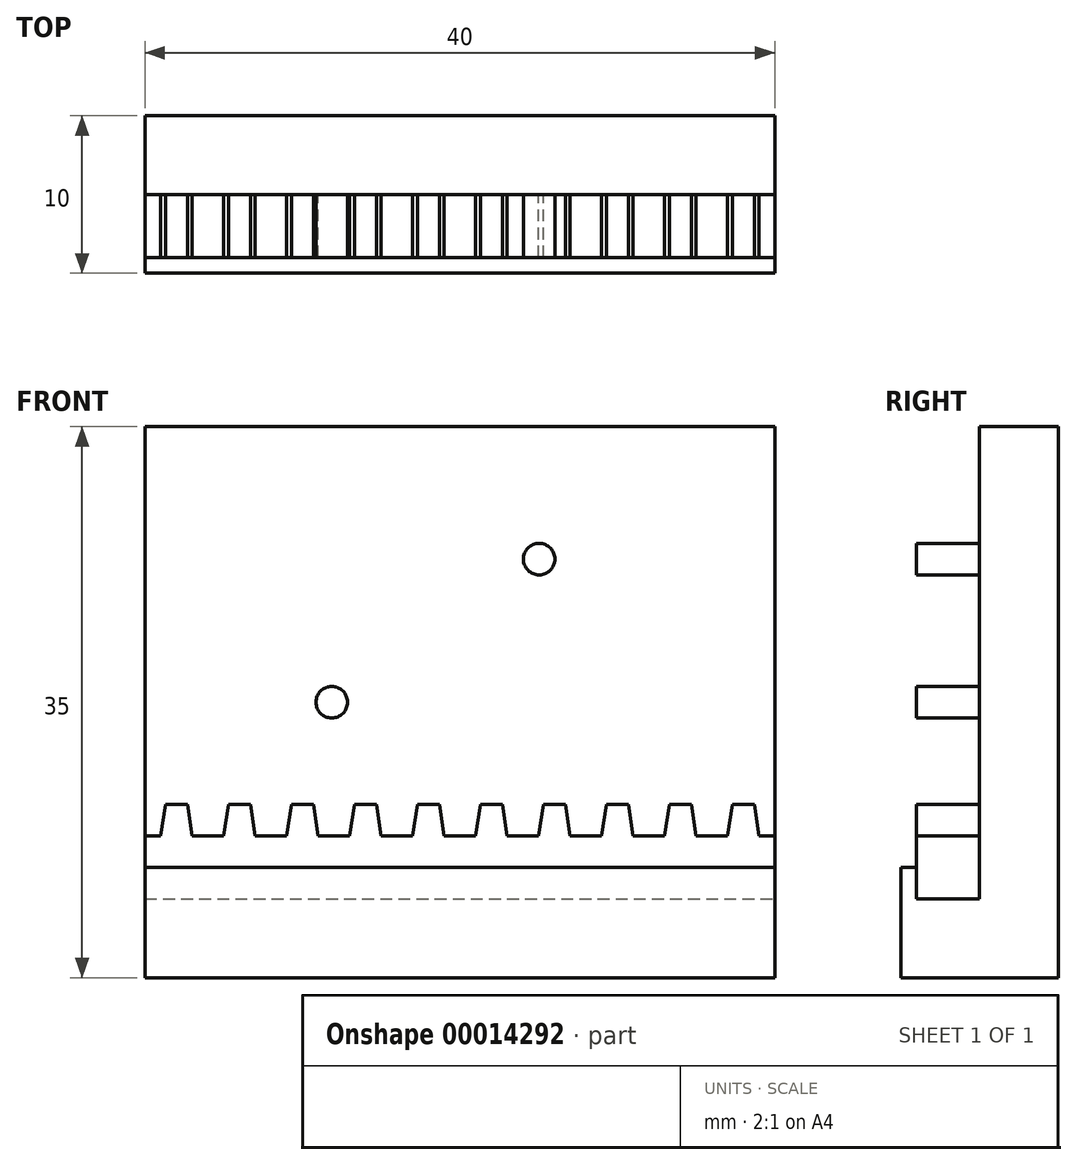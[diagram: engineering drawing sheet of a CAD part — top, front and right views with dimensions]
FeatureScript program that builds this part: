
annotation { "Feature Type Name" : "Feature", "Feature Type Description" : "" }
export const myFeature = defineFeature(function(context is Context, id is Id, definition is map)
    precondition{}
    {
        {
            var Q0;
            Q0=qCreatedBy(makeId("Front.planeOp"),FACE);
            var sketch = newSketch(context, id + "F0", { "sketchPlane" : qUnion([Q0])});
            skLineSegment(sketch, "E0.rect.bottom", {"start": v(20, -17.5) * mm, "end": v(-20, -17.5) * mm});
            skLineSegment(sketch, "E0.rect.top", {"start": v(20, 17.5) * mm, "end": v(-20, 17.5) * mm});
            skLineSegment(sketch, "E0.rect.left", {"start": v(20, -17.5) * mm, "end": v(20, 17.5) * mm});
            skLineSegment(sketch, "E0.rect.right", {"start": v(-20, -17.5) * mm, "end": v(-20, 17.5) * mm});
            skPoint(sketch, "E0.rect.middle", {"position": v(0, 0) * mm});
            skSolve(sketch);
        }
        {
            var Q0;
            Q0 = qSketchRegion(id + "F0", true);
            extrude(context, id + "F1", {"entities" : qUnion([Q0]), "depth" : 10 * mm});
        }
        {
            var Q0;
            Q0=makeQuery(id+"F1.opExtrude","CAP_FACE",FACE,{"disambiguationData":[OSD([sQuery(id+"F0.wireOp",EDGE,"E0.rect.bottom"),sQuery(id+"F0.wireOp",EDGE,"E0.rect.top"),sQuery(id+"F0.wireOp",EDGE,"E0.rect.left"),sQuery(id+"F0.wireOp",EDGE,"E0.rect.right")])],"isStart":false});
            var sketch = newSketch(context, id + "F2", { "sketchPlane" : qUnion([Q0])});
            skLineSegment(sketch, "E1.bottom", {"start": v(-20, 17.5) * mm, "end": v(20, 17.5) * mm});
            skLineSegment(sketch, "E1.top", {"start": v(-20, -12.5) * mm, "end": v(20, -12.5) * mm});
            skLineSegment(sketch, "E1.left", {"start": v(-20, 17.5) * mm, "end": v(-20, -12.5) * mm});
            skLineSegment(sketch, "E1.right", {"start": v(20, 17.5) * mm, "end": v(20, -12.5) * mm});
            skSolve(sketch);
        }
        {
            var Q0;
            Q0 = qSketchRegion(id + "F2", true);
            extrude(context, id + "F3", {"entities" : qUnion([Q0]), "operationType" : NewBodyOperationType.REMOVE, "oppositeDirection" : true, "depth" : 5 * mm});
        }
        {
            var Q0;
            Q0=makeQuery(id+"F1.opExtrude","SWEPT_FACE",FACE,{"disambiguationData":[OSD([sQuery(id+"F0.wireOp",EDGE,"E0.rect.left")])]});
            var sketch = newSketch(context, id + "F4", { "sketchPlane" : qUnion([Q0])});
            skLineSegment(sketch, "E2.bottom", {"start": v(-10, -12.5) * mm, "end": v(-9, -12.5) * mm});
            skLineSegment(sketch, "E2.top", {"start": v(-10, -10.5) * mm, "end": v(-9, -10.5) * mm});
            skLineSegment(sketch, "E2.left", {"start": v(-10, -12.5) * mm, "end": v(-10, -10.5) * mm});
            skLineSegment(sketch, "E2.right", {"start": v(-9, -12.5) * mm, "end": v(-9, -10.5) * mm});
            skSolve(sketch);
        }
        {
            var Q0;
            Q0 = qSketchRegion(id + "F4", true);
            var Q1;
            Q1=makeQuery(id+"F1.opExtrude","SWEPT_FACE",FACE,{"disambiguationData":[OSD([sQuery(id+"F0.wireOp",EDGE,"E0.rect.right")])]});
            extrude(context, id + "F5", {"entities" : qUnion([Q0]), "operationType" : NewBodyOperationType.ADD, "endBound" : BoundingType.UP_TO_SURFACE, "oppositeDirection" : true, "endBoundEntityFace" : qUnion([Q1]), "depth" : 25 * mm});
        }
        {
            var Q0;
            Q0=makeQuery(id+"F3.boolean.opBoolean","COPY",FACE,{"derivedFrom":makeQuery(id+"F3.opExtrude","CAP_FACE",FACE,{"disambiguationData":[OSD([sQuery(id+"F2.wireOp",EDGE,"E1.bottom"),sQuery(id+"F2.wireOp",EDGE,"E1.top"),sQuery(id+"F2.wireOp",EDGE,"E1.left"),sQuery(id+"F2.wireOp",EDGE,"E1.right")])],"isStart":false})});
            var sketch = newSketch(context, id + "F6", { "sketchPlane" : qUnion([Q0])});
            skCircle(sketch, "E3", {"center": v(-8.14, 0) * mm, "radius": 1 * mm});
            skCircle(sketch, "E4", {"center": v(5.04, 9.09) * mm, "radius": 1 * mm});
            skSolve(sketch);
        }
        {
            var Q0;
            Q0 = qSketchRegion(id + "F6", true);
            extrude(context, id + "F7", {"entities" : qUnion([Q0]), "operationType" : NewBodyOperationType.ADD, "depth" : 4 * mm});
        }
        {
            var Q0;
            Q0=makeQuery(id+"F3.boolean.opBoolean","COPY",FACE,{"derivedFrom":makeQuery(id+"F3.opExtrude","CAP_FACE",FACE,{"disambiguationData":[OSD([sQuery(id+"F2.wireOp",EDGE,"E1.bottom"),sQuery(id+"F2.wireOp",EDGE,"E1.top"),sQuery(id+"F2.wireOp",EDGE,"E1.left"),sQuery(id+"F2.wireOp",EDGE,"E1.right")])],"isStart":false})});
            var sketch = newSketch(context, id + "F8", { "sketchPlane" : qUnion([Q0])});
            skLineSegment(sketch, "E5.bottom", {"start": v(20, -8.5) * mm, "end": v(-20, -8.5) * mm});
            skLineSegment(sketch, "E5.top", {"start": v(20, -12.5) * mm, "end": v(-20, -12.5) * mm});
            skLineSegment(sketch, "E5.left", {"start": v(20, -8.5) * mm, "end": v(20, -12.5) * mm});
            skLineSegment(sketch, "E5.right", {"start": v(-20, -8.5) * mm, "end": v(-20, -12.5) * mm});
            skLineSegment(sketch, "E6", {"start": v(-18, -8.5) * mm, "end": v(-18, -12.5) * mm, "construction": true});
            skLineSegment(sketch, "E7", {"start": v(-19, -8.5) * mm, "end": v(-18.7, -6.5) * mm});
            skLineSegment(sketch, "E8", {"start": v(-18.7, -6.5) * mm, "end": v(-18, -6.5) * mm});
            skLineSegment(sketch, "E9.MirrorCS", {"start": v(-17, -8.5) * mm, "end": v(-17.3, -6.5) * mm});
            skLineSegment(sketch, "E10.MirrorCS", {"start": v(-17.3, -6.5) * mm, "end": v(-18, -6.5) * mm});
            skLineSegment(sketch, "E11.1.0.0", {"start": v(-15, -8.5) * mm, "end": v(-14.7, -6.5) * mm});
            skLineSegment(sketch, "E11.1.0.1", {"start": v(-14.7, -6.5) * mm, "end": v(-14, -6.5) * mm});
            skLineSegment(sketch, "E11.1.0.2", {"start": v(-13.3, -6.5) * mm, "end": v(-14, -6.5) * mm});
            skLineSegment(sketch, "E11.1.0.3", {"start": v(-13, -8.5) * mm, "end": v(-13.3, -6.5) * mm});
            skLineSegment(sketch, "E11.2.0.0", {"start": v(-11, -8.5) * mm, "end": v(-10.7, -6.5) * mm});
            skLineSegment(sketch, "E11.2.0.1", {"start": v(-10.7, -6.5) * mm, "end": v(-10, -6.5) * mm});
            skLineSegment(sketch, "E11.2.0.2", {"start": v(-9.3, -6.5) * mm, "end": v(-10, -6.5) * mm});
            skLineSegment(sketch, "E11.2.0.3", {"start": v(-9, -8.5) * mm, "end": v(-9.3, -6.5) * mm});
            skLineSegment(sketch, "E11.3.0.0", {"start": v(-7, -8.5) * mm, "end": v(-6.7, -6.5) * mm});
            skLineSegment(sketch, "E11.3.0.1", {"start": v(-6.7, -6.5) * mm, "end": v(-6, -6.5) * mm});
            skLineSegment(sketch, "E11.3.0.2", {"start": v(-5.3, -6.5) * mm, "end": v(-6, -6.5) * mm});
            skLineSegment(sketch, "E11.3.0.3", {"start": v(-5, -8.5) * mm, "end": v(-5.3, -6.5) * mm});
            skLineSegment(sketch, "E11.4.0.0", {"start": v(-3, -8.5) * mm, "end": v(-2.7, -6.5) * mm});
            skLineSegment(sketch, "E11.4.0.1", {"start": v(-2.7, -6.5) * mm, "end": v(-2, -6.5) * mm});
            skLineSegment(sketch, "E11.4.0.2", {"start": v(-1.3, -6.5) * mm, "end": v(-2, -6.5) * mm});
            skLineSegment(sketch, "E11.4.0.3", {"start": v(-1, -8.5) * mm, "end": v(-1.3, -6.5) * mm});
            skLineSegment(sketch, "E11.5.0.0", {"start": v(1, -8.5) * mm, "end": v(1.3, -6.5) * mm});
            skLineSegment(sketch, "E11.5.0.1", {"start": v(1.3, -6.5) * mm, "end": v(2, -6.5) * mm});
            skLineSegment(sketch, "E11.5.0.2", {"start": v(2.7, -6.5) * mm, "end": v(2, -6.5) * mm});
            skLineSegment(sketch, "E11.5.0.3", {"start": v(3, -8.5) * mm, "end": v(2.7, -6.5) * mm});
            skLineSegment(sketch, "E11.6.0.0", {"start": v(5, -8.5) * mm, "end": v(5.3, -6.5) * mm});
            skLineSegment(sketch, "E11.6.0.1", {"start": v(5.3, -6.5) * mm, "end": v(6, -6.5) * mm});
            skLineSegment(sketch, "E11.6.0.2", {"start": v(6.7, -6.5) * mm, "end": v(6, -6.5) * mm});
            skLineSegment(sketch, "E11.6.0.3", {"start": v(7, -8.5) * mm, "end": v(6.7, -6.5) * mm});
            skLineSegment(sketch, "E11.7.0.0", {"start": v(9, -8.5) * mm, "end": v(9.3, -6.5) * mm});
            skLineSegment(sketch, "E11.7.0.1", {"start": v(9.3, -6.5) * mm, "end": v(10, -6.5) * mm});
            skLineSegment(sketch, "E11.7.0.2", {"start": v(10.7, -6.5) * mm, "end": v(10, -6.5) * mm});
            skLineSegment(sketch, "E11.7.0.3", {"start": v(11, -8.5) * mm, "end": v(10.7, -6.5) * mm});
            skLineSegment(sketch, "E11.8.0.0", {"start": v(13, -8.5) * mm, "end": v(13.3, -6.5) * mm});
            skLineSegment(sketch, "E11.8.0.1", {"start": v(13.3, -6.5) * mm, "end": v(14, -6.5) * mm});
            skLineSegment(sketch, "E11.8.0.2", {"start": v(14.7, -6.5) * mm, "end": v(14, -6.5) * mm});
            skLineSegment(sketch, "E11.8.0.3", {"start": v(15, -8.5) * mm, "end": v(14.7, -6.5) * mm});
            skLineSegment(sketch, "E11.9.0.0", {"start": v(17, -8.5) * mm, "end": v(17.3, -6.5) * mm});
            skLineSegment(sketch, "E11.9.0.1", {"start": v(17.3, -6.5) * mm, "end": v(18, -6.5) * mm});
            skLineSegment(sketch, "E11.9.0.2", {"start": v(18.7, -6.5) * mm, "end": v(18, -6.5) * mm});
            skLineSegment(sketch, "E11.9.0.3", {"start": v(19, -8.5) * mm, "end": v(18.7, -6.5) * mm});
            skLineSegment(sketch, "E11.direction1", {"start": v(-19, -8.5) * mm, "end": v(-15, -8.5) * mm, "construction": true});
            skSolve(sketch);
        }
        {
            var Q0;
            Q0 = qSketchRegion(id + "F8", true);
            extrude(context, id + "F9", {"entities" : qUnion([Q0]), "depth" : 4 * mm});
        }
    });
